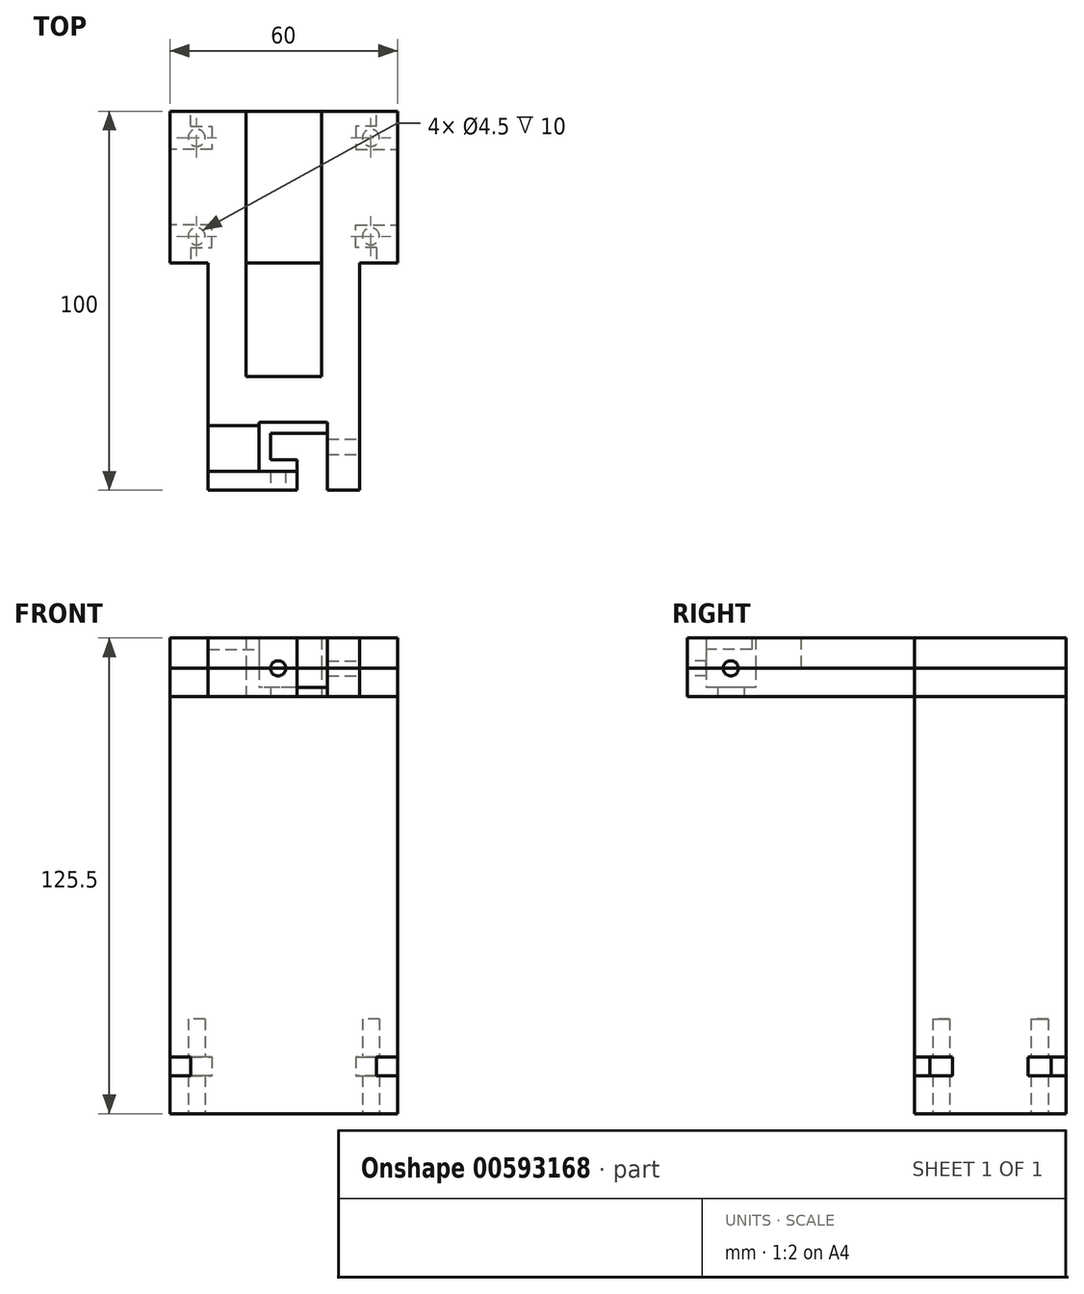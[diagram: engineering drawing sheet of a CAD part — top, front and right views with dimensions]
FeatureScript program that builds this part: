
annotation { "Feature Type Name" : "Feature", "Feature Type Description" : "" }
export const myFeature = defineFeature(function(context is Context, id is Id, definition is map)
    precondition{}
    {
        {
            var Q0;
            Q0=qCreatedBy(makeId("Top.planeOp"),FACE);
            var sketch = newSketch(context, id + "F0", { "sketchPlane" : qUnion([Q0])});
            skLineSegment(sketch, "E0.bottom", {"start": v(-30, 20) * mm, "end": v(30, 20) * mm});
            skLineSegment(sketch, "E0.top", {"start": v(-30, -20) * mm, "end": v(30, -20) * mm});
            skLineSegment(sketch, "E0.left", {"start": v(-30, 20) * mm, "end": v(-30, -20) * mm});
            skLineSegment(sketch, "E0.right", {"start": v(30, 20) * mm, "end": v(30, -20) * mm});
            skCircle(sketch, "E1", {"center": v(-23, 13) * mm, "radius": 2.25 * mm});
            skCircle(sketch, "E2.MirrorC", {"center": v(23, 13) * mm, "radius": 2.25 * mm});
            skCircle(sketch, "E3.MirrorC", {"center": v(-23, -13) * mm, "radius": 2.25 * mm});
            skCircle(sketch, "E4.MirrorC", {"center": v(23, -13) * mm, "radius": 2.25 * mm});
            skSolve(sketch);
        }
        {
            var Q0;
            Q0 = qSketchRegion(id + "F0", true);
            extrude(context, id + "F1", {"entities" : qUnion([Q0]), "depth" : 10 * mm, "offsetDistance" : 25 * mm});
        }
        {
            var Q0;
            Q0=makeQuery(id+"F1.opExtrude","CAP_FACE",FACE,{"disambiguationData":[OSD([sQuery(id+"F0.wireOp",EDGE,"E0.bottom"),sQuery(id+"F0.wireOp",EDGE,"E0.top"),sQuery(id+"F0.wireOp",EDGE,"E0.left"),sQuery(id+"F0.wireOp",EDGE,"E0.right"),sQuery(id+"F0.wireOp",EDGE,"E1"),sQuery(id+"F0.wireOp",EDGE,"E2.MirrorC"),sQuery(id+"F0.wireOp",EDGE,"E3.MirrorC"),sQuery(id+"F0.wireOp",EDGE,"E4.MirrorC")])],"isStart":false});
            var sketch = newSketch(context, id + "F2", { "sketchPlane" : qUnion([Q0])});
            skLineSegment(sketch, "E5.0", {"start": v(-19, 16) * mm, "end": v(-19, 10) * mm});
            skLineSegment(sketch, "E5.3", {"start": v(-24.5, 16) * mm, "end": v(-19, 16) * mm});
            skLineSegment(sketch, "E6", {"start": v(-24.5, 16) * mm, "end": v(-24.5, 20) * mm});
            skLineSegment(sketch, "E7", {"start": v(-19, 10) * mm, "end": v(-30, 10) * mm});
            skLineSegment(sketch, "E8.MirrorCS", {"start": v(19, 10) * mm, "end": v(30, 10) * mm});
            skLineSegment(sketch, "E9.MirrorCS", {"start": v(19, 16) * mm, "end": v(19, 10) * mm});
            skLineSegment(sketch, "E10.MirrorCS", {"start": v(24.5, 16) * mm, "end": v(24.5, 20) * mm});
            skLineSegment(sketch, "E11.MirrorCS", {"start": v(24.5, 16) * mm, "end": v(19, 16) * mm});
            skLineSegment(sketch, "E12.MirrorCS", {"start": v(-19, -16) * mm, "end": v(-19, -10) * mm});
            skLineSegment(sketch, "E13.MirrorCS", {"start": v(-19, -10) * mm, "end": v(-30, -10) * mm});
            skLineSegment(sketch, "E14.MirrorCS", {"start": v(-24.5, -16) * mm, "end": v(-24.5, -20) * mm});
            skLineSegment(sketch, "E15.MirrorCS", {"start": v(-24.5, -16) * mm, "end": v(-19, -16) * mm});
            skLineSegment(sketch, "E16.MirrorCS", {"start": v(24.5, -16) * mm, "end": v(24.5, -20) * mm});
            skLineSegment(sketch, "E17.MirrorCS", {"start": v(19, -16) * mm, "end": v(19, -10) * mm});
            skLineSegment(sketch, "E18.MirrorCS", {"start": v(19, -10) * mm, "end": v(30, -10) * mm});
            skLineSegment(sketch, "E19.MirrorCS", {"start": v(24.5, -16) * mm, "end": v(19, -16) * mm});
            skSolve(sketch);
        }
        {
            var Q0;
            Q0=makeQuery(id+"F2.imprint","IMPRINT",FACE,{"disambiguationData":[TD([[makeQuery(id+"F2.imprint","IMPRINT",EDGE,{"derivedFrom":sQuery(id+"F2.wireOp",EDGE,"E5.0")}),1.0]])]});
            extrude(context, id + "F3", {"entities" : qUnion([Q0]), "operationType" : NewBodyOperationType.ADD, "depth" : 5 * mm, "offsetDistance" : 25 * mm});
        }
        {
            var Q0;
            Q0=makeQuery(id+"F3.opExtrude","CAP_FACE",FACE,{"disambiguationData":[OSD([sQuery(id+"F0.wireOp",EDGE,"E0.bottom"),sQuery(id+"F0.wireOp",EDGE,"E0.top"),sQuery(id+"F0.wireOp",EDGE,"E0.left"),sQuery(id+"F0.wireOp",EDGE,"E0.right"),sQuery(id+"F2.wireOp",EDGE,"E5.0"),sQuery(id+"F2.wireOp",EDGE,"E5.3"),sQuery(id+"F2.wireOp",EDGE,"E6"),sQuery(id+"F2.wireOp",EDGE,"E7"),sQuery(id+"F2.wireOp",EDGE,"E8.MirrorCS"),sQuery(id+"F2.wireOp",EDGE,"E9.MirrorCS"),sQuery(id+"F2.wireOp",EDGE,"E10.MirrorCS"),sQuery(id+"F2.wireOp",EDGE,"E11.MirrorCS"),sQuery(id+"F2.wireOp",EDGE,"E12.MirrorCS"),sQuery(id+"F2.wireOp",EDGE,"E13.MirrorCS"),sQuery(id+"F2.wireOp",EDGE,"E14.MirrorCS"),sQuery(id+"F2.wireOp",EDGE,"E15.MirrorCS"),sQuery(id+"F2.wireOp",EDGE,"E16.MirrorCS"),sQuery(id+"F2.wireOp",EDGE,"E17.MirrorCS"),sQuery(id+"F2.wireOp",EDGE,"E18.MirrorCS"),sQuery(id+"F2.wireOp",EDGE,"E19.MirrorCS")])],"isStart":false});
            var sketch = newSketch(context, id + "F4", { "sketchPlane" : qUnion([Q0])});
            skLineSegment(sketch, "E20.bottom", {"start": v(-30, 20) * mm, "end": v(30, 20) * mm});
            skLineSegment(sketch, "E20.top", {"start": v(-30, -20) * mm, "end": v(30, -20) * mm});
            skLineSegment(sketch, "E20.left", {"start": v(-30, 20) * mm, "end": v(-30, -20) * mm});
            skLineSegment(sketch, "E20.right", {"start": v(30, 20) * mm, "end": v(30, -20) * mm});
            skCircle(sketch, "E21", {"center": v(-23, 13) * mm, "radius": 2.25 * mm});
            skCircle(sketch, "E22.MirrorC", {"center": v(23, 13) * mm, "radius": 2.25 * mm});
            skCircle(sketch, "E23.MirrorC", {"center": v(-23, -13) * mm, "radius": 2.25 * mm});
            skCircle(sketch, "E24.MirrorC", {"center": v(23, -13) * mm, "radius": 2.25 * mm});
            skSolve(sketch);
        }
        {
            var Q0;
            Q0 = qSketchRegion(id + "F4", true);
            extrude(context, id + "F5", {"entities" : qUnion([Q0]), "operationType" : NewBodyOperationType.ADD, "depth" : 10 * mm, "offsetDistance" : 25 * mm});
        }
        {
            var Q0;
            Q0=makeQuery(id+"F5.opExtrude","CAP_FACE",FACE,{"disambiguationData":[OSD([sQuery(id+"F4.wireOp",EDGE,"E20.bottom"),sQuery(id+"F4.wireOp",EDGE,"E20.top"),sQuery(id+"F4.wireOp",EDGE,"E20.left"),sQuery(id+"F4.wireOp",EDGE,"E20.right"),sQuery(id+"F4.wireOp",EDGE,"E21"),sQuery(id+"F4.wireOp",EDGE,"E22.MirrorC"),sQuery(id+"F4.wireOp",EDGE,"E23.MirrorC"),sQuery(id+"F4.wireOp",EDGE,"E24.MirrorC")])],"isStart":false});
            var sketch = newSketch(context, id + "F6", { "sketchPlane" : qUnion([Q0])});
            skLineSegment(sketch, "E25.bottom", {"start": v(30, -20) * mm, "end": v(-30, -20) * mm});
            skLineSegment(sketch, "E25.top", {"start": v(30, 20) * mm, "end": v(-30, 20) * mm});
            skLineSegment(sketch, "E25.left", {"start": v(30, -20) * mm, "end": v(30, 20) * mm});
            skLineSegment(sketch, "E25.right", {"start": v(-30, -20) * mm, "end": v(-30, 20) * mm});
            skSolve(sketch);
        }
        {
            var Q0;
            Q0 = qSketchRegion(id + "F6", true);
            extrude(context, id + "F7", {"entities" : qUnion([Q0]), "operationType" : NewBodyOperationType.ADD, "depth" : 85 * mm, "offsetDistance" : 25 * mm});
        }
        {
            var Q0;
            Q0=makeQuery(id+"F7.opExtrude","CAP_FACE",FACE,{"disambiguationData":[OSD([sQuery(id+"F6.wireOp",EDGE,"E25.bottom"),sQuery(id+"F6.wireOp",EDGE,"E25.top"),sQuery(id+"F6.wireOp",EDGE,"E25.left"),sQuery(id+"F6.wireOp",EDGE,"E25.right")])],"isStart":false});
            var sketch = newSketch(context, id + "F8", { "sketchPlane" : qUnion([Q0])});
            skLineSegment(sketch, "E26.bottom", {"start": v(-30, 20) * mm, "end": v(-10, 20) * mm});
            skLineSegment(sketch, "E26.top", {"start": v(-30, -20) * mm, "end": v(-20, -20) * mm});
            skLineSegment(sketch, "E26.left", {"start": v(-30, 20) * mm, "end": v(-30, -20) * mm});
            skLineSegment(sketch, "E26.right", {"start": v(-10, 20) * mm, "end": v(-10, -20) * mm});
            skLineSegment(sketch, "E27.bottom", {"start": v(30, 20) * mm, "end": v(10, 20) * mm});
            skLineSegment(sketch, "E27.top", {"start": v(30, -20) * mm, "end": v(20, -20) * mm});
            skLineSegment(sketch, "E27.left", {"start": v(30, 20) * mm, "end": v(30, -20) * mm});
            skLineSegment(sketch, "E27.right", {"start": v(10, 20) * mm, "end": v(10, -20) * mm});
            skLineSegment(sketch, "E28", {"start": v(-20, -20) * mm, "end": v(-20, -80) * mm});
            skLineSegment(sketch, "E29", {"start": v(-20, -80) * mm, "end": v(3.5, -80) * mm});
            skLineSegment(sketch, "E30", {"start": v(20, -80) * mm, "end": v(20, -20) * mm});
            skLineSegment(sketch, "E31.top", {"start": v(3.5, -65) * mm, "end": v(11.5, -65) * mm});
            skLineSegment(sketch, "E31.left", {"start": v(3.5, -72) * mm, "end": v(3.5, -80) * mm});
            skLineSegment(sketch, "E31.right", {"start": v(11.5, -80) * mm, "end": v(11.5, -65) * mm});
            skLineSegment(sketch, "E32.trimOffspring", {"start": v(11.5, -80) * mm, "end": v(20, -80) * mm});
            skLineSegment(sketch, "E33.bottom", {"start": v(3.5, -65) * mm, "end": v(-3.5, -65) * mm});
            skLineSegment(sketch, "E33.top", {"start": v(3.5, -72) * mm, "end": v(-3.5, -72) * mm});
            skLineSegment(sketch, "E33.right", {"start": v(-3.5, -65) * mm, "end": v(-3.5, -72) * mm});
            skSolve(sketch);
        }
        {
            var Q0;
            Q0 = qSketchRegion(id + "F8", true);
            var Q1;
            Q1=makeQuery(id+"F8.imprint","IMPRINT",FACE,{"disambiguationData":[TD([[makeQuery(id+"F8.imprint","IMPRINT",EDGE,{"derivedFrom":sQuery(id+"F8.wireOp",EDGE,"E26.bottom")}),-1.0]])]});
            var Q2;
            Q2=makeQuery(id+"F8.imprint","IMPRINT",FACE,{"disambiguationData":[TD([[makeQuery(id+"F8.imprint","IMPRINT",EDGE,{"derivedFrom":sQuery(id+"F8.wireOp",EDGE,"E27.bottom")}),-1.0]])]});
            var Q3;
            {var subQ0=sQuery(id+"F8.wireOp",EDGE,"E28");Q3=makeQuery(id+"F8.imprint","IMPRINT",FACE,{"disambiguationData":[TD([[makeQuery(id+"F8.imprint","IMPRINT",EDGE,{"derivedFrom":subQ0}),1.0]])]});}
            extrude(context, id + "F9", {"entities" : qUnion([Q0, Q1, Q2, Q3]), "depth" : 2.5 * mm, "offsetDistance" : 25 * mm});
        }
        {
            var Q0;
            Q0=makeQuery(id+"F9.opExtrude","CAP_FACE",FACE,{"disambiguationData":[OSD([sQuery(id+"F6.wireOp",EDGE,"E25.bottom"),sQuery(id+"F8.wireOp",EDGE,"E26.bottom"),sQuery(id+"F8.wireOp",EDGE,"E26.top"),sQuery(id+"F8.wireOp",EDGE,"E26.left"),sQuery(id+"F8.wireOp",EDGE,"E26.right"),sQuery(id+"F8.wireOp",EDGE,"E27.bottom"),sQuery(id+"F8.wireOp",EDGE,"E27.top"),sQuery(id+"F8.wireOp",EDGE,"E27.left"),sQuery(id+"F8.wireOp",EDGE,"E27.right"),sQuery(id+"F8.wireOp",EDGE,"E28"),sQuery(id+"F8.wireOp",EDGE,"E29"),sQuery(id+"F8.wireOp",EDGE,"E30"),sQuery(id+"F8.wireOp",EDGE,"E31.top"),sQuery(id+"F8.wireOp",EDGE,"E31.left"),sQuery(id+"F8.wireOp",EDGE,"E31.right"),sQuery(id+"F8.wireOp",EDGE,"E32.trimOffspring"),sQuery(id+"F8.wireOp",EDGE,"E33.bottom"),sQuery(id+"F8.wireOp",EDGE,"E33.top"),sQuery(id+"F8.wireOp",EDGE,"E33.right")])],"isStart":false});
            var sketch = newSketch(context, id + "F10", { "sketchPlane" : qUnion([Q0])});
            skLineSegment(sketch, "E34.0", {"start": v(3.5, -62) * mm, "end": v(11.5, -62) * mm});
            skLineSegment(sketch, "E34.1", {"start": v(3.5, -62) * mm, "end": v(-6.5, -62) * mm});
            skLineSegment(sketch, "E34.2", {"start": v(-6.5, -62) * mm, "end": v(-6.5, -75) * mm});
            skLineSegment(sketch, "E34.3", {"start": v(3.5, -75) * mm, "end": v(-6.5, -75) * mm});
            skLineSegment(sketch, "E35", {"start": v(11.5, -62) * mm, "end": v(11.5, -65) * mm});
            skLineSegment(sketch, "E36", {"start": v(11.5, -65) * mm, "end": v(11.5, -80) * mm});
            skLineSegment(sketch, "E37", {"start": v(3.5, -75) * mm, "end": v(3.5, -80) * mm});
            skSolve(sketch);
        }
        {
            var Q0;
            Q0=makeQuery(id+"F10.imprint","IMPRINT",FACE,{"disambiguationData":[TD([[makeQuery(id+"F10.imprint","IMPRINT",EDGE,{"derivedFrom":sQuery(id+"F10.wireOp",EDGE,"E34.0")}),1.0]])]});
            extrude(context, id + "F11", {"entities" : qUnion([Q0]), "operationType" : NewBodyOperationType.ADD, "depth" : 5 * mm, "offsetDistance" : 25 * mm});
        }
        {
            var Q0;
            Q0=makeQuery(id+"F11.opExtrude","CAP_FACE",FACE,{"disambiguationData":[OSD([sQuery(id+"F6.wireOp",EDGE,"E25.bottom"),sQuery(id+"F8.wireOp",EDGE,"E26.bottom"),sQuery(id+"F8.wireOp",EDGE,"E26.top"),sQuery(id+"F8.wireOp",EDGE,"E26.left"),sQuery(id+"F8.wireOp",EDGE,"E26.right"),sQuery(id+"F8.wireOp",EDGE,"E27.bottom"),sQuery(id+"F8.wireOp",EDGE,"E27.top"),sQuery(id+"F8.wireOp",EDGE,"E27.left"),sQuery(id+"F8.wireOp",EDGE,"E27.right"),sQuery(id+"F8.wireOp",EDGE,"E28"),sQuery(id+"F8.wireOp",EDGE,"E29"),sQuery(id+"F8.wireOp",EDGE,"E30"),sQuery(id+"F8.wireOp",EDGE,"E32.trimOffspring"),sQuery(id+"F10.wireOp",EDGE,"E34.0"),sQuery(id+"F10.wireOp",EDGE,"E34.1"),sQuery(id+"F10.wireOp",EDGE,"E34.2"),sQuery(id+"F10.wireOp",EDGE,"E34.3"),sQuery(id+"F10.wireOp",EDGE,"E35"),sQuery(id+"F10.wireOp",EDGE,"E36"),sQuery(id+"F10.wireOp",EDGE,"E37")])],"isStart":false});
            var sketch = newSketch(context, id + "F12", { "sketchPlane" : qUnion([Q0])});
            skLineSegment(sketch, "E38.top", {"start": v(-10, -50) * mm, "end": v(10, -50) * mm});
            skLineSegment(sketch, "E38.left", {"start": v(-10, -20) * mm, "end": v(-10, -50) * mm});
            skLineSegment(sketch, "E38.right", {"start": v(10, -20) * mm, "end": v(10, -50) * mm});
            skSolve(sketch);
        }
        {
            var Q0;
            Q0=makeQuery(id+"F12.imprint","IMPRINT",FACE,{"disambiguationData":[TD([[makeQuery(id+"F12.imprint","IMPRINT",EDGE,{"derivedFrom":sQuery(id+"F12.wireOp",EDGE,"E38.top")}),-1.0]])]});
            extrude(context, id + "F13", {"entities" : qUnion([Q0]), "depth" : 5 * mm, "offsetDistance" : 25 * mm});
        }
        {
            var Q0;
            Q0=makeQuery(id+"F13.opExtrude","CAP_FACE",FACE,{"disambiguationData":[OSD([sQuery(id+"F8.wireOp",EDGE,"E26.bottom"),sQuery(id+"F8.wireOp",EDGE,"E26.top"),sQuery(id+"F8.wireOp",EDGE,"E26.left"),sQuery(id+"F8.wireOp",EDGE,"E26.right"),sQuery(id+"F8.wireOp",EDGE,"E27.bottom"),sQuery(id+"F8.wireOp",EDGE,"E27.top"),sQuery(id+"F8.wireOp",EDGE,"E27.left"),sQuery(id+"F8.wireOp",EDGE,"E27.right"),sQuery(id+"F8.wireOp",EDGE,"E28"),sQuery(id+"F8.wireOp",EDGE,"E29"),sQuery(id+"F8.wireOp",EDGE,"E30"),sQuery(id+"F8.wireOp",EDGE,"E32.trimOffspring"),sQuery(id+"F10.wireOp",EDGE,"E34.0"),sQuery(id+"F10.wireOp",EDGE,"E34.1"),sQuery(id+"F10.wireOp",EDGE,"E34.2"),sQuery(id+"F10.wireOp",EDGE,"E34.3"),sQuery(id+"F10.wireOp",EDGE,"E35"),sQuery(id+"F10.wireOp",EDGE,"E36"),sQuery(id+"F10.wireOp",EDGE,"E37"),sQuery(id+"F12.wireOp",EDGE,"E38.top"),sQuery(id+"F12.wireOp",EDGE,"E38.left"),sQuery(id+"F12.wireOp",EDGE,"E38.right")])],"isStart":false});
            var sketch = newSketch(context, id + "F14", { "sketchPlane" : qUnion([Q0])});
            skLineSegment(sketch, "E39.bottom", {"start": v(-20, -63) * mm, "end": v(-6.5, -63) * mm});
            skLineSegment(sketch, "E39.top", {"start": v(-20, -75) * mm, "end": v(-6.5, -75) * mm});
            skSolve(sketch);
        }
        {
            var Q0;
            {var subQ2=sQuery(id+"F14.wireOp",EDGE,"E39.bottom");Q0=makeQuery(id+"F14.imprint","IMPRINT",FACE,{"disambiguationData":[TD([[makeQuery(id+"F14.imprint","IMPRINT",EDGE,{"derivedFrom":subQ2}),1.0]])]});}
            var Q1;
            {var subQ3=sQuery(id+"F14.wireOp",EDGE,"E39.top");Q1=makeQuery(id+"F14.imprint","IMPRINT",FACE,{"disambiguationData":[TD([[makeQuery(id+"F14.imprint","IMPRINT",EDGE,{"derivedFrom":subQ3}),-1.0]])]});}
            extrude(context, id + "F15", {"entities" : qUnion([Q0, Q1]), "operationType" : NewBodyOperationType.ADD, "depth" : 3 * mm, "offsetDistance" : 25 * mm});
        }
        {
            var Q0;
            {var subQ0=sQuery(id+"F8.wireOp",EDGE,"E30");Q0=makeQuery(id+"F11.boolean.opBoolean","MERGE",FACE,{"derivedFrom":[makeQuery(id+"F9.opExtrude","SWEPT_FACE",FACE,{"disambiguationData":[OSD([subQ0])]}),makeQuery(id+"F11.opExtrude","SWEPT_FACE",FACE,{"disambiguationData":[OSD([subQ0])]})]});}
            var sketch = newSketch(context, id + "F16", { "sketchPlane" : qUnion([Q0])});
            skCircle(sketch, "E40", {"center": v(-68.5, 117.5) * mm, "radius": 2 * mm});
            skSolve(sketch);
        }
        {
            var Q0;
            Q0 = qSketchRegion(id + "F16", true);
            extrude(context, id + "F17", {"entities" : qUnion([Q0]), "operationType" : NewBodyOperationType.REMOVE, "oppositeDirection" : true, "depth" : 10 * mm, "offsetDistance" : 25 * mm});
        }
        {
            var Q0;
            {var subQ0=sQuery(id+"F8.wireOp",EDGE,"E29");Q0=makeQuery(id+"F15.boolean.opBoolean","MERGE",FACE,{"derivedFrom":[makeQuery(id+"F13.opExtrude","SWEPT_FACE",FACE,{"disambiguationData":[OSD([subQ0])]}),makeQuery(id+"F15.opExtrude","SWEPT_FACE",FACE,{"disambiguationData":[OSD([subQ0])]})]});}
            var sketch = newSketch(context, id + "F18", { "sketchPlane" : qUnion([Q0])});
            skCircle(sketch, "E41", {"center": v(-1.5, 117.5) * mm, "radius": 2 * mm});
            skSolve(sketch);
        }
        {
            var Q0;
            Q0 = qSketchRegion(id + "F18", true);
            extrude(context, id + "F19", {"entities" : qUnion([Q0]), "operationType" : NewBodyOperationType.REMOVE, "oppositeDirection" : true, "depth" : 10 * mm, "offsetDistance" : 25 * mm});
        }
    });
